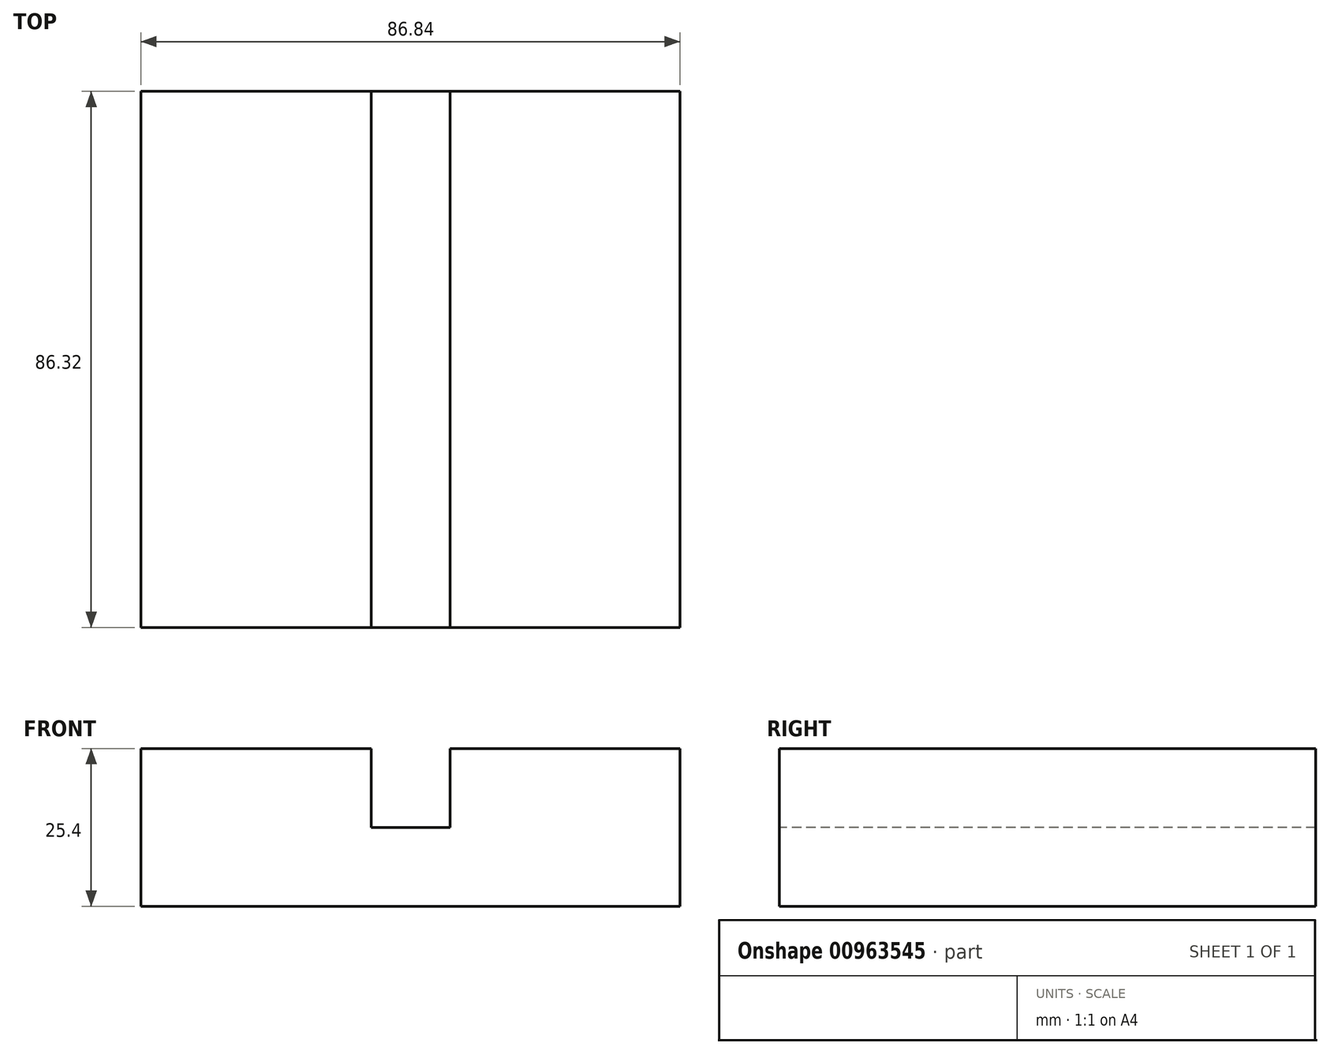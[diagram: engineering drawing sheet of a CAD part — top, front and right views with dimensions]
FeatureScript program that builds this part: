
annotation { "Feature Type Name" : "Feature", "Feature Type Description" : "" }
export const myFeature = defineFeature(function(context is Context, id is Id, definition is map)
    precondition{}
    {
        {
            var Q0;
            Q0=qCreatedBy(makeId("Top.planeOp"),FACE);
            var sketch = newSketch(context, id + "F0", { "sketchPlane" : qUnion([Q0])});
            skLineSegment(sketch, "E0.bottom", {"start": v(43.42, 43.16) * mm, "end": v(-43.42, 43.16) * mm});
            skLineSegment(sketch, "E0.top", {"start": v(43.42, -43.16) * mm, "end": v(-43.42, -43.16) * mm});
            skLineSegment(sketch, "E0.left", {"start": v(43.42, 43.16) * mm, "end": v(43.42, -43.16) * mm});
            skLineSegment(sketch, "E0.right", {"start": v(-43.42, 43.16) * mm, "end": v(-43.42, -43.16) * mm});
            skPoint(sketch, "E0.middle", {"position": v(0, 0) * mm});
            skSolve(sketch);
        }
        {
            var Q0;
            Q0=makeQuery(id+"F0.imprint","IMPRINT",FACE,{"disambiguationData":[TD([[makeQuery(id+"F0.imprint","IMPRINT",EDGE,{"derivedFrom":sQuery(id+"F0.wireOp",EDGE,"E0.bottom")}),1.0]])]});
            extrude(context, id + "F1", {"entities" : qUnion([Q0]), "depth" : 25.4 * mm, "offsetDistance" : 25.4 * mm});
        }
        {
            var Q0;
            Q0=makeQuery(id+"F1.opExtrude","CAP_FACE",FACE,{"disambiguationData":[OSD([sQuery(id+"F0.wireOp",EDGE,"E0.bottom"),sQuery(id+"F0.wireOp",EDGE,"E0.top"),sQuery(id+"F0.wireOp",EDGE,"E0.left"),sQuery(id+"F0.wireOp",EDGE,"E0.right")])],"isStart":false});
            var sketch = newSketch(context, id + "F2", { "sketchPlane" : qUnion([Q0])});
            skLineSegment(sketch, "E1", {"start": v(0, 43.16) * mm, "end": v(0, -43.16) * mm});
            skArc(sketch, "E2.0.startCap", {"start": v(-6.35, 43.16) * mm, "mid": v(0, 49.5) * mm, "end": v(6.35, 43.16) * mm});
            skArc(sketch, "E2.0.endCap", {"start": v(6.35, -43.16) * mm, "mid": v(0, -49.5) * mm, "end": v(-6.35, -43.16) * mm});
            skLineSegment(sketch, "E2.0.left", {"start": v(6.35, 43.16) * mm, "end": v(6.35, -43.16) * mm});
            skLineSegment(sketch, "E2.0.right", {"start": v(-6.35, 43.16) * mm, "end": v(-6.35, -43.16) * mm});
            skSolve(sketch);
        }
        {
            var Q0;
            Q0 = qSketchRegion(id + "F2", true);
            extrude(context, id + "F3", {"entities" : qUnion([Q0]), "operationType" : NewBodyOperationType.REMOVE, "oppositeDirection" : true, "depth" : 12.7 * mm, "offsetDistance" : 25.4 * mm});
        }
    });
